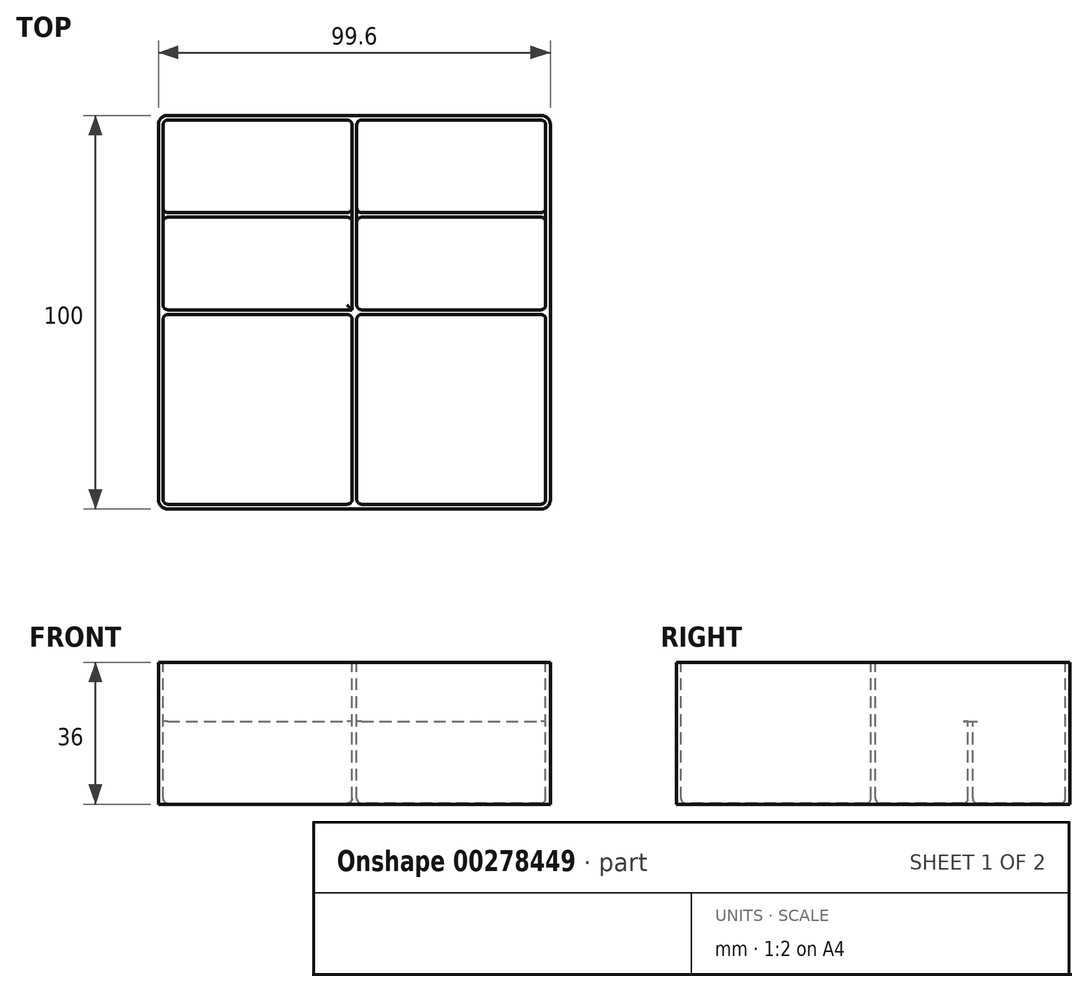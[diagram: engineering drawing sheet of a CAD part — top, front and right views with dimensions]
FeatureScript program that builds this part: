
annotation { "Feature Type Name" : "Feature", "Feature Type Description" : "" }
export const myFeature = defineFeature(function(context is Context, id is Id, definition is map)
    precondition{}
    {
        {
            var Q0;
            Q0=qCreatedBy(makeId("Top.planeOp"),FACE);
            var sketch = newSketch(context, id + "F0", { "sketchPlane" : qUnion([Q0])});
            skLineSegment(sketch, "E0.bottom", {"start": v(115.5, -50) * mm, "end": v(-115.5, -50) * mm});
            skLineSegment(sketch, "E0.top", {"start": v(115.5, 50) * mm, "end": v(-115.5, 50) * mm});
            skLineSegment(sketch, "E0.left", {"start": v(115.5, -50) * mm, "end": v(115.5, 50) * mm});
            skLineSegment(sketch, "E0.right", {"start": v(-115.5, -50) * mm, "end": v(-115.5, 50) * mm});
            skPoint(sketch, "E0.middle", {"position": v(0, 0) * mm});
            skSolve(sketch);
        }
        {
            var Q0;
            Q0 = qSketchRegion(id + "F0", true);
            extrude(context, id + "F1", {"entities" : qUnion([Q0]), "depth" : 36 * mm});
        }
        {
            var Q0;
            Q0=makeQuery(id+"F1.opExtrude","CAP_FACE",FACE,{"disambiguationData":[OSD([sQuery(id+"F0.wireOp",EDGE,"E0.bottom"),sQuery(id+"F0.wireOp",EDGE,"E0.top"),sQuery(id+"F0.wireOp",EDGE,"E0.left"),sQuery(id+"F0.wireOp",EDGE,"E0.right")])],"isStart":false});
            var sketch = newSketch(context, id + "F2", { "sketchPlane" : qUnion([Q0])});
            skLineSegment(sketch, "E1.bottom", {"start": v(114.3, 48.8) * mm, "end": v(66.3, 48.8) * mm});
            skLineSegment(sketch, "E1.top", {"start": v(114.3, 0.6) * mm, "end": v(66.3, 0.6) * mm});
            skLineSegment(sketch, "E1.left", {"start": v(114.3, 48.8) * mm, "end": v(114.3, 0.6) * mm});
            skLineSegment(sketch, "E1.right", {"start": v(66.3, 48.8) * mm, "end": v(66.3, 0.6) * mm});
            skLineSegment(sketch, "E2.bottom", {"start": v(114.3, -0.6) * mm, "end": v(66.3, -0.6) * mm});
            skLineSegment(sketch, "E2.top", {"start": v(114.3, -48.8) * mm, "end": v(66.3, -48.8) * mm});
            skLineSegment(sketch, "E2.left", {"start": v(114.3, -0.6) * mm, "end": v(114.3, -48.8) * mm});
            skLineSegment(sketch, "E2.right", {"start": v(66.3, -0.6) * mm, "end": v(66.3, -48.8) * mm});
            skLineSegment(sketch, "E3.bottom", {"start": v(65.1, 48.8) * mm, "end": v(17.1, 48.8) * mm});
            skLineSegment(sketch, "E3.top", {"start": v(65.1, 0.6) * mm, "end": v(17.1, 0.6) * mm});
            skLineSegment(sketch, "E3.left", {"start": v(65.1, 48.8) * mm, "end": v(65.1, 0.6) * mm});
            skLineSegment(sketch, "E3.right", {"start": v(17.1, 48.8) * mm, "end": v(17.1, 0.6) * mm});
            skLineSegment(sketch, "E4.bottom", {"start": v(65.1, -48.8) * mm, "end": v(17.1, -48.8) * mm});
            skLineSegment(sketch, "E4.top", {"start": v(65.1, -0.6) * mm, "end": v(17.1, -0.6) * mm});
            skLineSegment(sketch, "E4.left", {"start": v(65.1, -48.8) * mm, "end": v(65.1, -0.6) * mm});
            skLineSegment(sketch, "E4.right", {"start": v(17.1, -48.8) * mm, "end": v(17.1, -0.6) * mm});
            skLineSegment(sketch, "E5", {"start": v(17.1, 24.7) * mm, "end": v(114.3, 24.7) * mm});
            skLineSegment(sketch, "E6.0", {"start": v(17.1, 24.1) * mm, "end": v(121.34, 24.1) * mm});
            skLineSegment(sketch, "E7.0", {"start": v(17.1, 25.3) * mm, "end": v(115.07, 25.3) * mm});
            skSolve(sketch);
        }
        {
            var Q0;
            {var subQ0=sQuery(id+"F2.wireOp",EDGE,"E3.bottom");Q0=makeQuery(id+"F2.imprint","IMPRINT",FACE,{"disambiguationData":[TD([[makeQuery(id+"F2.imprint","IMPRINT",EDGE,{"derivedFrom":subQ0}),1.0]])]});}
            var Q1;
            {var subQ0=sQuery(id+"F2.wireOp",EDGE,"E1.bottom");Q1=makeQuery(id+"F2.imprint","IMPRINT",FACE,{"disambiguationData":[TD([[makeQuery(id+"F2.imprint","IMPRINT",EDGE,{"derivedFrom":subQ0}),1.0]])]});}
            var Q2;
            {var subQ0=sQuery(id+"F2.wireOp",EDGE,"E3.top");Q2=makeQuery(id+"F2.imprint","IMPRINT",FACE,{"disambiguationData":[TD([[makeQuery(id+"F2.imprint","IMPRINT",EDGE,{"derivedFrom":subQ0}),-1.0]])]});}
            var Q3;
            {var subQ0=sQuery(id+"F2.wireOp",EDGE,"E1.top");Q3=makeQuery(id+"F2.imprint","IMPRINT",FACE,{"disambiguationData":[TD([[makeQuery(id+"F2.imprint","IMPRINT",EDGE,{"derivedFrom":subQ0}),-1.0]])]});}
            var Q4;
            Q4=makeQuery(id+"F2.imprint","IMPRINT",FACE,{"disambiguationData":[TD([[makeQuery(id+"F2.imprint","IMPRINT",EDGE,{"derivedFrom":sQuery(id+"F2.wireOp",EDGE,"E4.bottom")}),-1.0]])]});
            var Q5;
            Q5=makeQuery(id+"F2.imprint","IMPRINT",FACE,{"disambiguationData":[TD([[makeQuery(id+"F2.imprint","IMPRINT",EDGE,{"derivedFrom":sQuery(id+"F2.wireOp",EDGE,"E2.bottom")}),1.0]])]});
            extrude(context, id + "F3", {"entities" : qUnion([Q0, Q1, Q2, Q3, Q4, Q5]), "operationType" : NewBodyOperationType.REMOVE, "oppositeDirection" : true, "depth" : 35.8 * mm});
        }
        {
            var Q0;
            Q0=makeQuery(id+"F1.opExtrude","CAP_FACE",FACE,{"disambiguationData":[OSD([sQuery(id+"F0.wireOp",EDGE,"E0.bottom"),sQuery(id+"F0.wireOp",EDGE,"E0.top"),sQuery(id+"F0.wireOp",EDGE,"E0.left"),sQuery(id+"F0.wireOp",EDGE,"E0.right")])],"isStart":false});
            var sketch = newSketch(context, id + "F4", { "sketchPlane" : qUnion([Q0])});
            skLineSegment(sketch, "E8.bottom", {"start": v(17.1, 24.1) * mm, "end": v(65.1, 24.1) * mm});
            skLineSegment(sketch, "E8.top", {"start": v(17.1, 25.3) * mm, "end": v(65.1, 25.3) * mm});
            skLineSegment(sketch, "E8.left", {"start": v(17.1, 24.1) * mm, "end": v(17.1, 25.3) * mm});
            skLineSegment(sketch, "E8.right", {"start": v(65.1, 24.1) * mm, "end": v(65.1, 25.3) * mm});
            skLineSegment(sketch, "E9.bottom", {"start": v(66.3, 24.1) * mm, "end": v(114.3, 24.1) * mm});
            skLineSegment(sketch, "E9.top", {"start": v(66.3, 25.3) * mm, "end": v(114.3, 25.3) * mm});
            skLineSegment(sketch, "E9.left", {"start": v(66.3, 24.1) * mm, "end": v(66.3, 25.3) * mm});
            skLineSegment(sketch, "E9.right", {"start": v(114.3, 24.1) * mm, "end": v(114.3, 25.3) * mm});
            skSolve(sketch);
        }
        {
            var Q0;
            Q0 = qSketchRegion(id + "F4", true);
            extrude(context, id + "F5", {"entities" : qUnion([Q0]), "operationType" : NewBodyOperationType.REMOVE, "oppositeDirection" : true, "depth" : 15 * mm});
        }
        {
            var Q0;
            Q0=makeQuery(id+"F1.opExtrude","CAP_FACE",FACE,{"disambiguationData":[OSD([sQuery(id+"F0.wireOp",EDGE,"E0.bottom"),sQuery(id+"F0.wireOp",EDGE,"E0.top"),sQuery(id+"F0.wireOp",EDGE,"E0.left"),sQuery(id+"F0.wireOp",EDGE,"E0.right")])],"isStart":false});
            var sketch = newSketch(context, id + "F6", { "sketchPlane" : qUnion([Q0])});
            skLineSegment(sketch, "E10.bottom", {"start": v(-114.3, 48.8) * mm, "end": v(-66.3, 48.8) * mm});
            skLineSegment(sketch, "E10.top", {"start": v(-114.3, -48.8) * mm, "end": v(-66.3, -48.8) * mm});
            skLineSegment(sketch, "E10.left", {"start": v(-114.3, 48.8) * mm, "end": v(-114.3, -48.8) * mm});
            skLineSegment(sketch, "E10.right", {"start": v(-66.3, 48.8) * mm, "end": v(-66.3, -48.8) * mm});
            skLineSegment(sketch, "E11.bottom", {"start": v(-65.1, 48.8) * mm, "end": v(15.9, 48.8) * mm});
            skLineSegment(sketch, "E11.top", {"start": v(-65.1, -48.8) * mm, "end": v(15.9, -48.8) * mm});
            skLineSegment(sketch, "E11.left", {"start": v(-65.1, 48.8) * mm, "end": v(-65.1, -48.8) * mm});
            skLineSegment(sketch, "E11.right", {"start": v(15.9, 48.8) * mm, "end": v(15.9, -48.8) * mm});
            skSolve(sketch);
        }
        {
            var Q0;
            Q0 = qSketchRegion(id + "F6", true);
            extrude(context, id + "F7", {"entities" : qUnion([Q0]), "operationType" : NewBodyOperationType.REMOVE, "oppositeDirection" : true, "depth" : 35.8 * mm});
        }
        {
            var Q0;
            Q0=makeQuery(id+"F1.opExtrude","SWEPT_EDGE",EDGE,{"disambiguationData":[OSD([sQuery(id+"F0.wireOp",EDGE,"E0.bottom"),sQuery(id+"F0.wireOp",EDGE,"E0.right")])]});
            var Q1;
            Q1=makeQuery(id+"F1.opExtrude","SWEPT_EDGE",EDGE,{"disambiguationData":[OSD([sQuery(id+"F0.wireOp",EDGE,"E0.top"),sQuery(id+"F0.wireOp",EDGE,"E0.right")])]});
            var Q2;
            Q2=makeQuery(id+"F1.opExtrude","SWEPT_EDGE",EDGE,{"disambiguationData":[OSD([sQuery(id+"F0.wireOp",EDGE,"E0.top"),sQuery(id+"F0.wireOp",EDGE,"E0.left")])]});
            var Q3;
            Q3=makeQuery(id+"F1.opExtrude","SWEPT_EDGE",EDGE,{"disambiguationData":[OSD([sQuery(id+"F0.wireOp",EDGE,"E0.bottom"),sQuery(id+"F0.wireOp",EDGE,"E0.left")])]});
            fillet(context, id + "F8", {"entities" : qUnion([Q0, Q1, Q2, Q3]), "radius" : 2.4 * mm, "tangentPropagation" : true, "allowEdgeOverflow" : false});
        }
        {
            var Q0;
            Q0=makeQuery(id+"F7.boolean.opBoolean","COPY",FACE,{"derivedFrom":makeQuery(id+"F7.opExtrude","CAP_FACE",FACE,{"disambiguationData":[OSD([sQuery(id+"F6.wireOp",EDGE,"E10.bottom"),sQuery(id+"F6.wireOp",EDGE,"E10.top"),sQuery(id+"F6.wireOp",EDGE,"E10.left"),sQuery(id+"F6.wireOp",EDGE,"E10.right")])],"isStart":false})});
            var Q1;
            Q1=makeQuery(id+"F7.boolean.opBoolean","COPY",FACE,{"derivedFrom":makeQuery(id+"F7.opExtrude","CAP_FACE",FACE,{"disambiguationData":[OSD([sQuery(id+"F6.wireOp",EDGE,"E11.bottom"),sQuery(id+"F6.wireOp",EDGE,"E11.top"),sQuery(id+"F6.wireOp",EDGE,"E11.left"),sQuery(id+"F6.wireOp",EDGE,"E11.right")])],"isStart":false})});
            var Q2;
            Q2=makeQuery(id+"F3.boolean.opBoolean","COPY",FACE,{"derivedFrom":makeQuery(id+"F3.opExtrude","CAP_FACE",FACE,{"disambiguationData":[OSD([sQuery(id+"F2.wireOp",EDGE,"E3.bottom"),sQuery(id+"F2.wireOp",EDGE,"E3.left"),sQuery(id+"F2.wireOp",EDGE,"E3.right"),sQuery(id+"F2.wireOp",EDGE,"E7.0")])],"isStart":false})});
            var Q3;
            Q3=makeQuery(id+"F3.boolean.opBoolean","COPY",FACE,{"derivedFrom":makeQuery(id+"F3.opExtrude","CAP_FACE",FACE,{"disambiguationData":[OSD([sQuery(id+"F2.wireOp",EDGE,"E1.bottom"),sQuery(id+"F2.wireOp",EDGE,"E1.left"),sQuery(id+"F2.wireOp",EDGE,"E1.right"),sQuery(id+"F2.wireOp",EDGE,"E7.0")])],"isStart":false})});
            var Q4;
            Q4=makeQuery(id+"F3.boolean.opBoolean","COPY",FACE,{"derivedFrom":makeQuery(id+"F3.opExtrude","CAP_FACE",FACE,{"disambiguationData":[OSD([sQuery(id+"F2.wireOp",EDGE,"E3.top"),sQuery(id+"F2.wireOp",EDGE,"E3.left"),sQuery(id+"F2.wireOp",EDGE,"E3.right"),sQuery(id+"F2.wireOp",EDGE,"E6.0")])],"isStart":false})});
            var Q5;
            Q5=makeQuery(id+"F3.boolean.opBoolean","COPY",FACE,{"derivedFrom":makeQuery(id+"F3.opExtrude","CAP_FACE",FACE,{"disambiguationData":[OSD([sQuery(id+"F2.wireOp",EDGE,"E1.top"),sQuery(id+"F2.wireOp",EDGE,"E1.left"),sQuery(id+"F2.wireOp",EDGE,"E1.right"),sQuery(id+"F2.wireOp",EDGE,"E6.0")])],"isStart":false})});
            var Q6;
            Q6=makeQuery(id+"F3.boolean.opBoolean","COPY",FACE,{"derivedFrom":makeQuery(id+"F3.opExtrude","CAP_FACE",FACE,{"disambiguationData":[OSD([sQuery(id+"F2.wireOp",EDGE,"E4.bottom"),sQuery(id+"F2.wireOp",EDGE,"E4.top"),sQuery(id+"F2.wireOp",EDGE,"E4.left"),sQuery(id+"F2.wireOp",EDGE,"E4.right")])],"isStart":false})});
            var Q7;
            Q7=makeQuery(id+"F3.boolean.opBoolean","COPY",FACE,{"derivedFrom":makeQuery(id+"F3.opExtrude","CAP_FACE",FACE,{"disambiguationData":[OSD([sQuery(id+"F2.wireOp",EDGE,"E2.bottom"),sQuery(id+"F2.wireOp",EDGE,"E2.top"),sQuery(id+"F2.wireOp",EDGE,"E2.left"),sQuery(id+"F2.wireOp",EDGE,"E2.right")])],"isStart":false})});
            var Q8;
            Q8=makeQuery(id+"F7.boolean.opBoolean","COPY",EDGE,{"derivedFrom":makeQuery(id+"F7.opExtrude","SWEPT_EDGE",EDGE,{"disambiguationData":[OSD([sQuery(id+"F6.wireOp",EDGE,"E10.bottom"),sQuery(id+"F6.wireOp",EDGE,"E10.left")])]})});
            var Q9;
            Q9=makeQuery(id+"F7.boolean.opBoolean","COPY",EDGE,{"derivedFrom":makeQuery(id+"F7.opExtrude","SWEPT_EDGE",EDGE,{"disambiguationData":[OSD([sQuery(id+"F6.wireOp",EDGE,"E11.bottom"),sQuery(id+"F6.wireOp",EDGE,"E11.left")])]})});
            var Q10;
            Q10=makeQuery(id+"F7.boolean.opBoolean","COPY",EDGE,{"derivedFrom":makeQuery(id+"F7.opExtrude","SWEPT_EDGE",EDGE,{"disambiguationData":[OSD([sQuery(id+"F6.wireOp",EDGE,"E10.bottom"),sQuery(id+"F6.wireOp",EDGE,"E10.right")])]})});
            var Q11;
            Q11=makeQuery(id+"F7.boolean.opBoolean","COPY",EDGE,{"derivedFrom":makeQuery(id+"F7.opExtrude","SWEPT_EDGE",EDGE,{"disambiguationData":[OSD([sQuery(id+"F6.wireOp",EDGE,"E10.top"),sQuery(id+"F6.wireOp",EDGE,"E10.right")])]})});
            var Q12;
            Q12=makeQuery(id+"F7.boolean.opBoolean","COPY",EDGE,{"derivedFrom":makeQuery(id+"F7.opExtrude","SWEPT_EDGE",EDGE,{"disambiguationData":[OSD([sQuery(id+"F6.wireOp",EDGE,"E10.top"),sQuery(id+"F6.wireOp",EDGE,"E10.left")])]})});
            var Q13;
            Q13=makeQuery(id+"F7.boolean.opBoolean","COPY",EDGE,{"derivedFrom":makeQuery(id+"F7.opExtrude","SWEPT_EDGE",EDGE,{"disambiguationData":[OSD([sQuery(id+"F6.wireOp",EDGE,"E11.bottom"),sQuery(id+"F6.wireOp",EDGE,"E11.right")])]})});
            var Q14;
            Q14=makeQuery(id+"F7.boolean.opBoolean","COPY",EDGE,{"derivedFrom":makeQuery(id+"F7.opExtrude","SWEPT_EDGE",EDGE,{"disambiguationData":[OSD([sQuery(id+"F6.wireOp",EDGE,"E11.top"),sQuery(id+"F6.wireOp",EDGE,"E11.right")])]})});
            var Q15;
            Q15=makeQuery(id+"F7.boolean.opBoolean","COPY",EDGE,{"derivedFrom":makeQuery(id+"F7.opExtrude","SWEPT_EDGE",EDGE,{"disambiguationData":[OSD([sQuery(id+"F6.wireOp",EDGE,"E11.top"),sQuery(id+"F6.wireOp",EDGE,"E11.left")])]})});
            var Q16;
            Q16=makeQuery(id+"F3.boolean.opBoolean","COPY",EDGE,{"derivedFrom":makeQuery(id+"F3.opExtrude","SWEPT_EDGE",EDGE,{"disambiguationData":[OSD([sQuery(id+"F2.wireOp",EDGE,"E4.bottom"),sQuery(id+"F2.wireOp",EDGE,"E4.right")])]})});
            var Q17;
            Q17=makeQuery(id+"F3.boolean.opBoolean","COPY",EDGE,{"derivedFrom":makeQuery(id+"F3.opExtrude","SWEPT_EDGE",EDGE,{"disambiguationData":[OSD([sQuery(id+"F2.wireOp",EDGE,"E3.top"),sQuery(id+"F2.wireOp",EDGE,"E3.right")])]})});
            var Q18;
            Q18=makeQuery(id+"F3.boolean.opBoolean","COPY",EDGE,{"derivedFrom":makeQuery(id+"F3.opExtrude","SWEPT_EDGE",EDGE,{"disambiguationData":[OSD([sQuery(id+"F2.wireOp",EDGE,"E3.right"),sQuery(id+"F2.wireOp",EDGE,"E7.0")])]})});
            var Q19;
            Q19=makeQuery(id+"F3.boolean.opBoolean","COPY",EDGE,{"derivedFrom":makeQuery(id+"F3.opExtrude","SWEPT_EDGE",EDGE,{"disambiguationData":[OSD([sQuery(id+"F2.wireOp",EDGE,"E3.bottom"),sQuery(id+"F2.wireOp",EDGE,"E3.right")])]})});
            var Q20;
            Q20=makeQuery(id+"F3.boolean.opBoolean","COPY",EDGE,{"derivedFrom":makeQuery(id+"F3.opExtrude","SWEPT_EDGE",EDGE,{"disambiguationData":[OSD([sQuery(id+"F2.wireOp",EDGE,"E3.right"),sQuery(id+"F2.wireOp",EDGE,"E6.0")])]})});
            var Q21;
            Q21=makeQuery(id+"F3.boolean.opBoolean","COPY",EDGE,{"derivedFrom":makeQuery(id+"F3.opExtrude","SWEPT_EDGE",EDGE,{"disambiguationData":[OSD([sQuery(id+"F2.wireOp",EDGE,"E4.top"),sQuery(id+"F2.wireOp",EDGE,"E4.right")])]})});
            var Q22;
            Q22=makeQuery(id+"F3.boolean.opBoolean","COPY",EDGE,{"derivedFrom":makeQuery(id+"F3.opExtrude","SWEPT_EDGE",EDGE,{"disambiguationData":[OSD([sQuery(id+"F2.wireOp",EDGE,"E4.top"),sQuery(id+"F2.wireOp",EDGE,"E4.left")])]})});
            var Q23;
            Q23=makeQuery(id+"F3.boolean.opBoolean","COPY",EDGE,{"derivedFrom":makeQuery(id+"F3.opExtrude","SWEPT_EDGE",EDGE,{"disambiguationData":[OSD([sQuery(id+"F2.wireOp",EDGE,"E4.bottom"),sQuery(id+"F2.wireOp",EDGE,"E4.left")])]})});
            var Q24;
            Q24=makeQuery(id+"F3.boolean.opBoolean","COPY",EDGE,{"derivedFrom":makeQuery(id+"F3.opExtrude","SWEPT_EDGE",EDGE,{"disambiguationData":[OSD([sQuery(id+"F2.wireOp",EDGE,"E3.left"),sQuery(id+"F2.wireOp",EDGE,"E6.0")])]})});
            var Q25;
            Q25=makeQuery(id+"F3.boolean.opBoolean","COPY",EDGE,{"derivedFrom":makeQuery(id+"F3.opExtrude","SWEPT_EDGE",EDGE,{"disambiguationData":[OSD([sQuery(id+"F2.wireOp",EDGE,"E3.left"),sQuery(id+"F2.wireOp",EDGE,"E7.0")])]})});
            var Q26;
            Q26=makeQuery(id+"F3.boolean.opBoolean","COPY",EDGE,{"derivedFrom":makeQuery(id+"F3.opExtrude","SWEPT_EDGE",EDGE,{"disambiguationData":[OSD([sQuery(id+"F2.wireOp",EDGE,"E3.bottom"),sQuery(id+"F2.wireOp",EDGE,"E3.left")])]})});
            var Q27;
            Q27=makeQuery(id+"F3.boolean.opBoolean","COPY",EDGE,{"derivedFrom":makeQuery(id+"F3.opExtrude","SWEPT_EDGE",EDGE,{"disambiguationData":[OSD([sQuery(id+"F2.wireOp",EDGE,"E1.bottom"),sQuery(id+"F2.wireOp",EDGE,"E1.right")])]})});
            var Q28;
            Q28=makeQuery(id+"F3.boolean.opBoolean","COPY",EDGE,{"derivedFrom":makeQuery(id+"F3.opExtrude","SWEPT_EDGE",EDGE,{"disambiguationData":[OSD([sQuery(id+"F2.wireOp",EDGE,"E1.bottom"),sQuery(id+"F2.wireOp",EDGE,"E1.left")])]})});
            var Q29;
            Q29=makeQuery(id+"F3.boolean.opBoolean","COPY",EDGE,{"derivedFrom":makeQuery(id+"F3.opExtrude","SWEPT_EDGE",EDGE,{"disambiguationData":[OSD([sQuery(id+"F2.wireOp",EDGE,"E1.left"),sQuery(id+"F2.wireOp",EDGE,"E6.0")])]})});
            var Q30;
            Q30=makeQuery(id+"F3.boolean.opBoolean","COPY",EDGE,{"derivedFrom":makeQuery(id+"F3.opExtrude","SWEPT_EDGE",EDGE,{"disambiguationData":[OSD([sQuery(id+"F2.wireOp",EDGE,"E1.left"),sQuery(id+"F2.wireOp",EDGE,"E7.0")])]})});
            var Q31;
            Q31=makeQuery(id+"F3.boolean.opBoolean","COPY",EDGE,{"derivedFrom":makeQuery(id+"F3.opExtrude","SWEPT_EDGE",EDGE,{"disambiguationData":[OSD([sQuery(id+"F2.wireOp",EDGE,"E1.right"),sQuery(id+"F2.wireOp",EDGE,"E7.0")])]})});
            var Q32;
            Q32=makeQuery(id+"F3.boolean.opBoolean","COPY",EDGE,{"derivedFrom":makeQuery(id+"F3.opExtrude","SWEPT_EDGE",EDGE,{"disambiguationData":[OSD([sQuery(id+"F2.wireOp",EDGE,"E1.right"),sQuery(id+"F2.wireOp",EDGE,"E6.0")])]})});
            var Q33;
            Q33=makeQuery(id+"F3.boolean.opBoolean","COPY",EDGE,{"derivedFrom":makeQuery(id+"F3.opExtrude","SWEPT_EDGE",EDGE,{"disambiguationData":[OSD([sQuery(id+"F2.wireOp",EDGE,"E1.top"),sQuery(id+"F2.wireOp",EDGE,"E1.right")])]})});
            var Q34;
            Q34=makeQuery(id+"F3.boolean.opBoolean","COPY",EDGE,{"derivedFrom":makeQuery(id+"F3.opExtrude","SWEPT_EDGE",EDGE,{"disambiguationData":[OSD([sQuery(id+"F2.wireOp",EDGE,"E2.bottom"),sQuery(id+"F2.wireOp",EDGE,"E2.right")])]})});
            var Q35;
            Q35=makeQuery(id+"F3.boolean.opBoolean","COPY",EDGE,{"derivedFrom":makeQuery(id+"F3.opExtrude","SWEPT_EDGE",EDGE,{"disambiguationData":[OSD([sQuery(id+"F2.wireOp",EDGE,"E2.bottom"),sQuery(id+"F2.wireOp",EDGE,"E2.left")])]})});
            var Q36;
            Q36=makeQuery(id+"F3.boolean.opBoolean","COPY",EDGE,{"derivedFrom":makeQuery(id+"F3.opExtrude","SWEPT_EDGE",EDGE,{"disambiguationData":[OSD([sQuery(id+"F2.wireOp",EDGE,"E1.top"),sQuery(id+"F2.wireOp",EDGE,"E1.left")])]})});
            var Q37;
            Q37=makeQuery(id+"F3.boolean.opBoolean","COPY",EDGE,{"derivedFrom":makeQuery(id+"F3.opExtrude","SWEPT_EDGE",EDGE,{"disambiguationData":[OSD([sQuery(id+"F2.wireOp",EDGE,"E2.top"),sQuery(id+"F2.wireOp",EDGE,"E2.left")])]})});
            var Q38;
            Q38=makeQuery(id+"F3.boolean.opBoolean","COPY",EDGE,{"derivedFrom":makeQuery(id+"F3.opExtrude","SWEPT_EDGE",EDGE,{"disambiguationData":[OSD([sQuery(id+"F2.wireOp",EDGE,"E2.top"),sQuery(id+"F2.wireOp",EDGE,"E2.right")])]})});
            fillet(context, id + "F9", {"entities" : qUnion([Q0, Q1, Q2, Q3, Q4, Q5, Q6, Q7, Q8, Q9, Q10, Q11, Q12, Q13, Q14, Q15, Q16, Q17, Q18, Q19, Q20, Q21, Q22, Q23, Q24, Q25, Q26, Q27, Q28, Q29, Q30, Q31, Q32, Q33, Q34, Q35, Q36, Q37, Q38]), "radius" : 1.2 * mm, "tangentPropagation" : true, "allowEdgeOverflow" : false});
        }
        {
            var Q0;
            Q0=makeQuery(id+"F1.opExtrude","CAP_FACE",FACE,{"disambiguationData":[OSD([sQuery(id+"F0.wireOp",EDGE,"E0.bottom"),sQuery(id+"F0.wireOp",EDGE,"E0.top"),sQuery(id+"F0.wireOp",EDGE,"E0.left"),sQuery(id+"F0.wireOp",EDGE,"E0.right")])],"isStart":false});
            var sketch = newSketch(context, id + "F10", { "sketchPlane" : qUnion([Q0])});
            skLineSegment(sketch, "E12.bottom", {"start": v(15.9, 63.12) * mm, "end": v(-129.53, 63.12) * mm});
            skLineSegment(sketch, "E12.top", {"start": v(15.9, -81.43) * mm, "end": v(-129.53, -81.43) * mm});
            skLineSegment(sketch, "E12.left", {"start": v(15.9, 63.12) * mm, "end": v(15.9, -81.43) * mm});
            skLineSegment(sketch, "E12.right", {"start": v(-129.53, 63.12) * mm, "end": v(-129.53, -81.43) * mm});
            skSolve(sketch);
        }
        {
            var Q0;
            Q0 = qSketchRegion(id + "F10", true);
            extrude(context, id + "F11", {"entities" : qUnion([Q0]), "operationType" : NewBodyOperationType.REMOVE, "oppositeDirection" : true, "depth" : 40 * mm});
        }
        {
            var Q0;
            Q0=makeQuery(id+"F11.boolean.opBoolean","INTERSECT",EDGE,{"derivedFrom":[makeQuery(id+"F1.opExtrude","SWEPT_FACE",FACE,{"disambiguationData":[OSD([sQuery(id+"F0.wireOp",EDGE,"E0.top")])]}),makeQuery(id+"F11.opExtrude","SWEPT_FACE",FACE,{"disambiguationData":[OSD([sQuery(id+"F10.wireOp",EDGE,"E12.left")])]})]});
            var Q1;
            Q1=makeQuery(id+"F11.boolean.opBoolean","INTERSECT",EDGE,{"derivedFrom":[makeQuery(id+"F1.opExtrude","SWEPT_FACE",FACE,{"disambiguationData":[OSD([sQuery(id+"F0.wireOp",EDGE,"E0.bottom")])]}),makeQuery(id+"F11.opExtrude","SWEPT_FACE",FACE,{"disambiguationData":[OSD([sQuery(id+"F10.wireOp",EDGE,"E12.left")])]})]});
            fillet(context, id + "F12", {"entities" : qUnion([Q0, Q1]), "radius" : 2.4 * mm, "tangentPropagation" : true, "allowEdgeOverflow" : false});
        }
    });
